# Revit family: Shower-Base-Caroma Mayfair1
name_source: partatom
category: Plumbing Fixtures
revit_build: Autodesk Revit 2014 (Build: 20131024_2115(x64)
units: mm (PartAtom-declared; Revit-internal decimal feet)

## types (1)
- 900mm
    Assembly Code = C1030210
    CW Connection = No
    Cost = 909 $
    Default Elevation = 0 mm  [stored 0 ft]
    Description = Caroma Mayfair Shower Base
    HW Connection = No
    Height_ANZRS = 40 mm  [stored 0.131234 ft]
    Keynote = SHR
    Length_ANZRS = 914 mm
    Manufacturer = GWA Bathrooms & Kitchens
    Material_ANZRS = Acrylic-White-Caroma
    Model = 857560W
    ModifiedIssue_ANZRS = 20141003.01 $
    PlumbingMaterial_ANZRS = Acrylic-White-Caroma
    Type Comments = Plug & waste not included, three sided tiling flange, white only
    URL = http://www.caroma.com.au
    Vent Connection = No
    WFU = 2
    Waste = Metal-Chrome-Caroma
    Waste Connection = Yes
    Width_ANZRS = 914 mm

note: [stored X ft] marks values corroborated as IEEE doubles in the binary element streams (Revit-internal decimal feet)

## geometry (parser evidence)
native form markers: Blend x8, Sweep x2
no freeform markers — native parametric forms only
